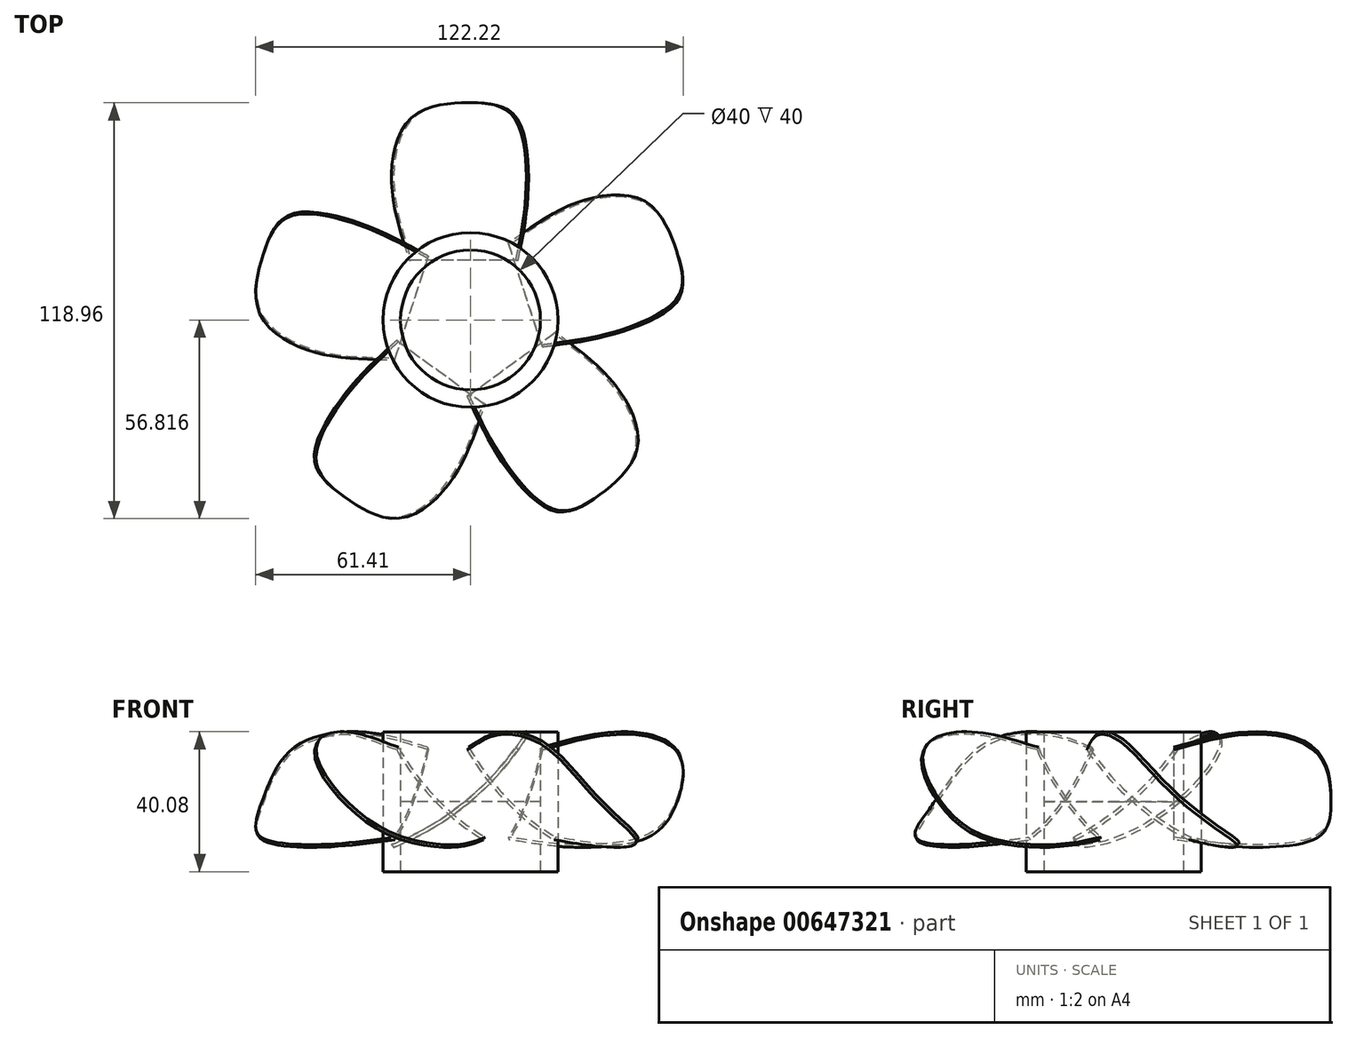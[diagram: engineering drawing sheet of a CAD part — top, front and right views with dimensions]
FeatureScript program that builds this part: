
annotation { "Feature Type Name" : "Feature", "Feature Type Description" : "" }
export const myFeature = defineFeature(function(context is Context, id is Id, definition is map)
    precondition{}
    {
        {
            var Q0;
            Q0=qCreatedBy(makeId("Top.planeOp"),FACE);
            var sketch = newSketch(context, id + "F0", { "sketchPlane" : qUnion([Q0])});
            skLineSegment(sketch, "E0.bottom", {"start": v(-20, 20) * mm, "end": v(20, 20) * mm, "construction": true});
            skLineSegment(sketch, "E0.top", {"start": v(-20, -20) * mm, "end": v(20, -20) * mm});
            skLineSegment(sketch, "E0.left", {"start": v(-20, 20) * mm, "end": v(-20, -20) * mm, "construction": true});
            skLineSegment(sketch, "E0.right", {"start": v(20, 20) * mm, "end": v(20, -20) * mm, "construction": true});
            skLineSegment(sketch, "E1", {"start": v(-20, 0) * mm, "end": v(20, 0) * mm, "construction": true});
            skLineSegment(sketch, "E2", {"start": v(0, 20) * mm, "end": v(0, -20) * mm, "construction": true});
            skFitSpline(sketch, "E3", {"points": [v(-20, -20) * mm, v(-25, 0) * mm, v(-20, 20) * mm, v(0, 25) * mm, v(20, 20) * mm, v(25, 0) * mm, v(20, -20) * mm], "startDerivative": vector(-33.55, 114.8) * mm, "endDerivative": vector(-38.64, -121.24) * mm});
            skLineSegment(sketch, "E4", {"start": v(-25, 0) * mm, "end": v(-20, 0) * mm, "construction": true});
            skLineSegment(sketch, "E5", {"start": v(0, 20) * mm, "end": v(0, 25) * mm, "construction": true});
            skLineSegment(sketch, "E6", {"start": v(20, 0) * mm, "end": v(25, 0) * mm, "construction": true});
            skSolve(sketch);
        }
        {
            var Q0;
            Q0=makeQuery(id+"F0.imprint","IMPRINT",FACE,{"disambiguationData":[TD([[makeQuery(id+"F0.imprint","IMPRINT",EDGE,{"derivedFrom":sQuery(id+"F0.wireOp",EDGE,"E0.top")}),1.0]])]});
            extrude(context, id + "F1", {"entities" : qUnion([Q0]), "endBound" : BoundingType.SYMMETRIC, "depth" : 20 * mm, "offsetDistance" : 25 * mm});
        }
        {
            var Q0;
            Q0=qCreatedBy(makeId("Front.planeOp"),FACE);
            var sketch = newSketch(context, id + "F2", { "sketchPlane" : qUnion([Q0])});
            skLineSegment(sketch, "E7", {"start": v(36.2, 0) * mm, "end": v(0, 0) * mm, "construction": true});
            skLineSegment(sketch, "E8", {"start": v(36.2, 0) * mm, "end": v(36.2, 62.13) * mm, "construction": true});
            skCircle(sketch, "E9", {"center": v(0, 81.07) * mm, "radius": 80 * mm});
            skLineSegment(sketch, "E10", {"start": v(0, 81.07) * mm, "end": v(0, 4.8) * mm, "construction": true});
            skLineSegment(sketch, "E11", {"start": v(0, 0) * mm, "end": v(0, 4.8) * mm, "construction": true});
            skLineSegment(sketch, "E12", {"start": v(23.97, 0) * mm, "end": v(23.97, 4.75) * mm, "construction": true});
            skLineSegment(sketch, "E13", {"start": v(23.97, 4.75) * mm, "end": v(0, 4.8) * mm, "construction": true});
            skLineSegment(sketch, "E14", {"start": v(0, 81.07) * mm, "end": v(0, 80.07) * mm, "construction": true});
            skCircle(sketch, "E15", {"center": v(0, 80.07) * mm, "radius": 80 * mm});
            skSolve(sketch);
        }
        {
            var Q0;
            {var subQ0=sQuery(id+"F2.wireOp",EDGE,"E15");var subQ1=sQuery(id+"F2.wireOp",EDGE,"E9");var subQ2=makeQuery(id+"F2.imprint","INTERSECT",VERTEX,{"disambiguationData":[OD(0.0)],"derivedFrom":[subQ1,subQ0]});Q0=makeQuery(id+"F2.imprint","IMPRINT",FACE,{"disambiguationData":[TD([[makeQuery(id+"F2.imprint","IMPRINT",EDGE,{"disambiguationData":[TD([[subQ2,-1.0]])],"derivedFrom":subQ1}),-1.0]])]});}
            extrude(context, id + "F3", {"entities" : qUnion([Q0]), "endBound" : BoundingType.SYMMETRIC, "depth" : 100 * mm, "offsetDistance" : 25 * mm});
        }
        {
            var Q0;
            Q0=makeQuery(id+"F3.opExtrude","SWEPT_BODY",BODY,{"disambiguationData":[OSD([sQuery(id+"F2.wireOp",EDGE,"E9"),sQuery(id+"F2.wireOp",EDGE,"E15")])]});
            var Q1;
            Q1=makeQuery(id+"F1.opExtrude","SWEPT_BODY",BODY,{"disambiguationData":[OSD([sQuery(id+"F0.wireOp",EDGE,"E0.top"),sQuery(id+"F0.wireOp",EDGE,"E3")])]});
            booleanBodies(context, id + "F4", {"operationType" : BooleanOperationType.INTERSECTION, "tools" : qUnion([Q0, Q1])});
        }
        {
            var Q0;
            Q0=makeQuery(id+"F4.opBoolean","INTERSECT",BODY,{"derivedFrom":[makeQuery(id+"F1.opExtrude","SWEPT_BODY",BODY,{"disambiguationData":[OSD([sQuery(id+"F0.wireOp",EDGE,"E0.top"),sQuery(id+"F0.wireOp",EDGE,"E3")])]}),makeQuery(id+"F3.opExtrude","SWEPT_BODY",BODY,{"disambiguationData":[OSD([sQuery(id+"F2.wireOp",EDGE,"E9"),sQuery(id+"F2.wireOp",EDGE,"E15")])]})]});
            var Q1;
            Q1=sQuery(id+"F0.wireOp",EDGE,"E2");
            transform(context, id + "F5", {"entities" : qUnion([Q0]), "transformType" : TransformType.ROTATION, "transformAxis" : qUnion([Q1]), "angle" : 40 * degree, "makeCopy" : false});
        }
        {
            var Q0;
            Q0=qCreatedBy(makeId("Top.planeOp"),FACE);
            var sketch = newSketch(context, id + "F6", { "sketchPlane" : qUnion([Q0])});
            skCircle(sketch, "E16", {"center": v(0, -37.14) * mm, "radius": 25 * mm});
            skCircle(sketch, "E17", {"center": v(0, -37.14) * mm, "radius": 20 * mm});
            skSolve(sketch);
        }
        {
            var Q0;
            Q0=makeQuery(id+"F6.imprint","IMPRINT",FACE,{"disambiguationData":[TD([[makeQuery(id+"F6.imprint","IMPRINT",EDGE,{"derivedFrom":sQuery(id+"F6.wireOp",EDGE,"E16")}),1.0]])]});
            extrude(context, id + "F7", {"entities" : qUnion([Q0]), "endBound" : BoundingType.SYMMETRIC, "depth" : 40 * mm, "offsetDistance" : 25 * mm});
        }
        {
            var Q0;
            Q0=makeQuery(id+"F6.imprint","IMPRINT",FACE,{"disambiguationData":[TD([[makeQuery(id+"F6.imprint","IMPRINT",EDGE,{"derivedFrom":sQuery(id+"F6.wireOp",EDGE,"E17")}),1.0]])]});
            extrude(context, id + "F8", {"entities" : qUnion([Q0]), "depth" : 20 * mm, "offsetDistance" : 25 * mm});
        }
        {
            var Q0;
            Q0=makeQuery(id+"F4.opBoolean","INTERSECT",BODY,{"derivedFrom":[makeQuery(id+"F1.opExtrude","SWEPT_BODY",BODY,{"disambiguationData":[OSD([sQuery(id+"F0.wireOp",EDGE,"E0.top"),sQuery(id+"F0.wireOp",EDGE,"E3")])]}),makeQuery(id+"F3.opExtrude","SWEPT_BODY",BODY,{"disambiguationData":[OSD([sQuery(id+"F2.wireOp",EDGE,"E9"),sQuery(id+"F2.wireOp",EDGE,"E15")])]})]});
            var Q1;
            Q1=sQuery(id+"F6.wireOp",EDGE,"E17");
            circularPattern(context, id + "F9", {"entities" : qUnion([Q0]), "axis" : qUnion([Q1]), "angle" : 360 * degree, "instanceCount" : 5, "equalSpace" : true});
        }
    });
